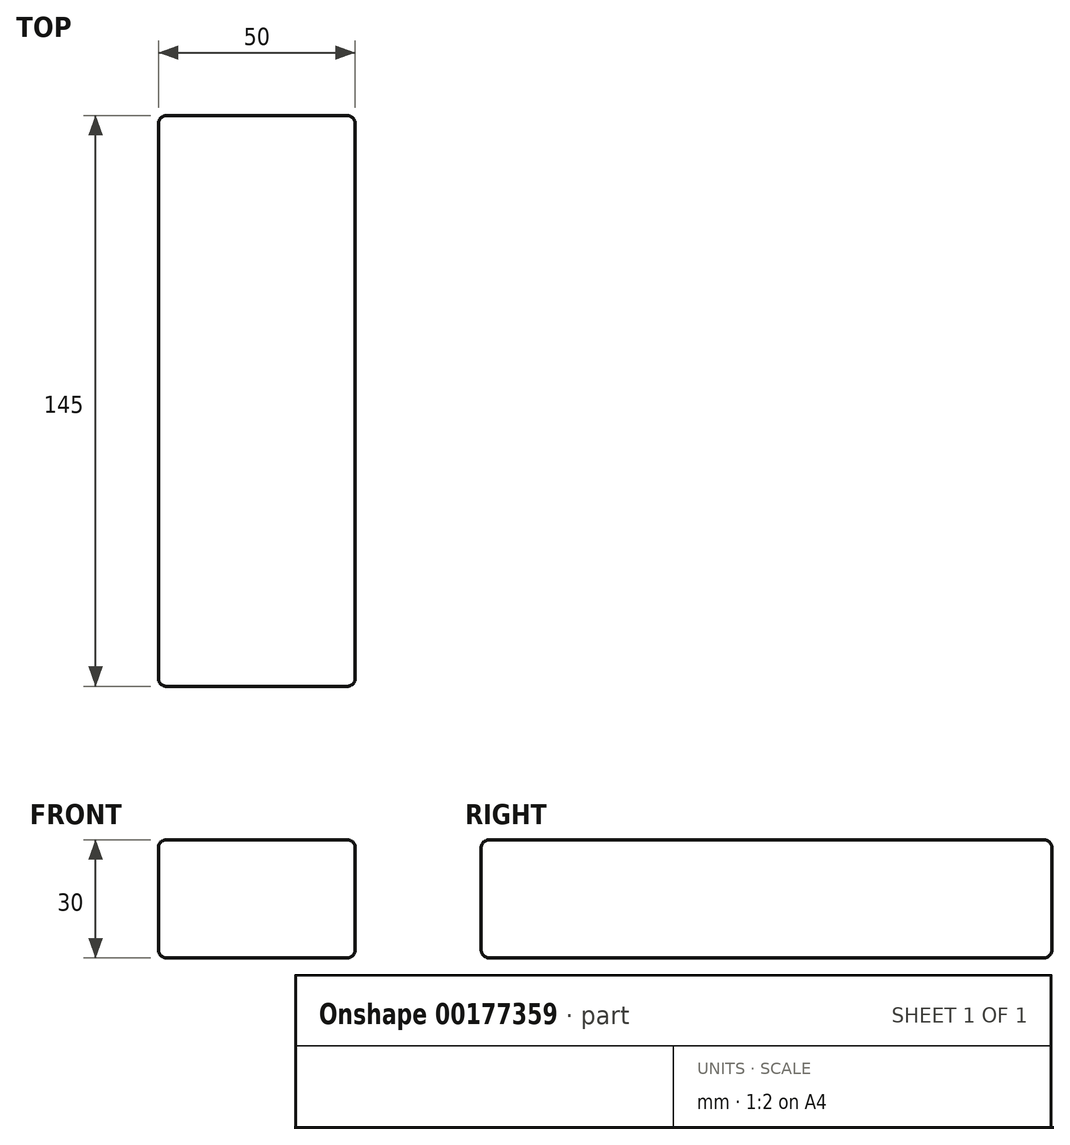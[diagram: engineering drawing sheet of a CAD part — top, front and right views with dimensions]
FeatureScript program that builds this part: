
annotation { "Feature Type Name" : "Feature", "Feature Type Description" : "" }
export const myFeature = defineFeature(function(context is Context, id is Id, definition is map)
    precondition{}
    {
        {
            var Q0;
            Q0=qCreatedBy(makeId("Front.planeOp"),FACE);
            var sketch = newSketch(context, id + "F0", { "sketchPlane" : qUnion([Q0])});
            skLineSegment(sketch, "E0.bottom", {"start": v(0, 0) * mm, "end": v(50, 0) * mm});
            skLineSegment(sketch, "E0.top", {"start": v(0, 30) * mm, "end": v(50, 30) * mm});
            skLineSegment(sketch, "E0.left", {"start": v(0, 0) * mm, "end": v(0, 30) * mm});
            skLineSegment(sketch, "E0.right", {"start": v(50, 0) * mm, "end": v(50, 30) * mm});
            skSolve(sketch);
        }
        {
            var Q0;
            Q0 = qSketchRegion(id + "F0", true);
            extrude(context, id + "F1", {"entities" : qUnion([Q0]), "depth" : 145 * mm, "offsetDistance" : 25 * mm});
        }
        {
            var Q0;
            Q0=makeQuery(id+"F1.opExtrude","SWEPT_FACE",FACE,{"disambiguationData":[OSD([sQuery(id+"F0.wireOp",EDGE,"E0.top")])]});
            var Q1;
            Q1=makeQuery(id+"F1.opExtrude","SWEPT_FACE",FACE,{"disambiguationData":[OSD([sQuery(id+"F0.wireOp",EDGE,"E0.bottom")])]});
            var Q2;
            Q2=makeQuery(id+"F1.opExtrude","SWEPT_FACE",FACE,{"disambiguationData":[OSD([sQuery(id+"F0.wireOp",EDGE,"E0.right")])]});
            var Q3;
            Q3=makeQuery(id+"F1.opExtrude","SWEPT_FACE",FACE,{"disambiguationData":[OSD([sQuery(id+"F0.wireOp",EDGE,"E0.left")])]});
            fillet(context, id + "F2", {"entities" : qUnion([Q0, Q1, Q2, Q3]), "radius" : 2 * mm, "tangentPropagation" : true, "allowEdgeOverflow" : false});
        }
    });
